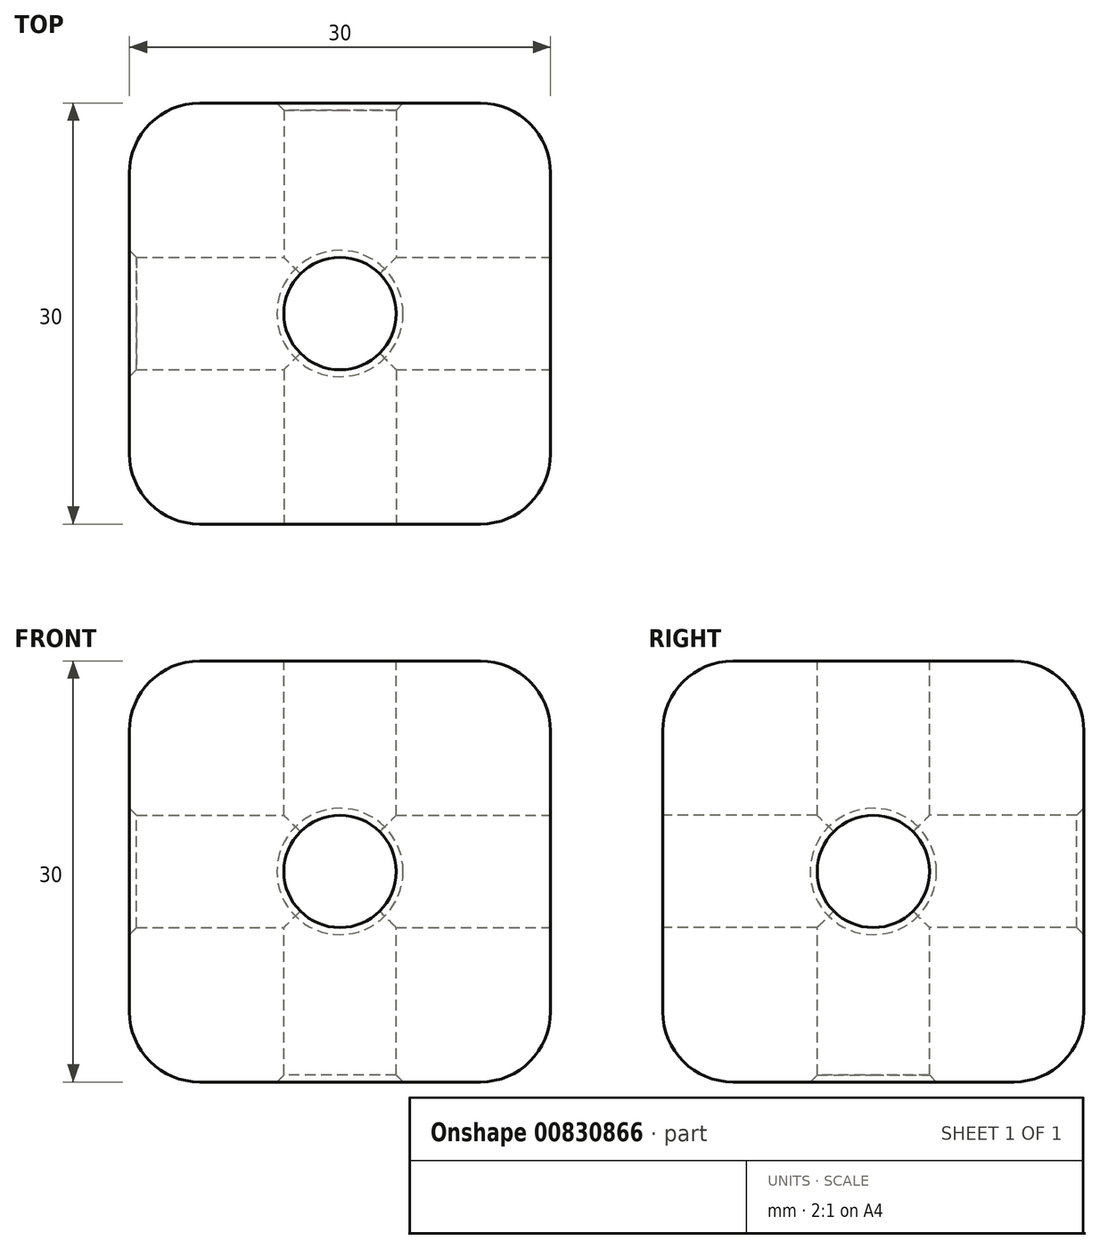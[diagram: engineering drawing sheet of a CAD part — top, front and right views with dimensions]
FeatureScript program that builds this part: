
annotation { "Feature Type Name" : "Feature", "Feature Type Description" : "" }
export const myFeature = defineFeature(function(context is Context, id is Id, definition is map)
    precondition{}
    {
        {
            var Q0;
            Q0=qCreatedBy(makeId("Front.planeOp"),FACE);
            var sketch = newSketch(context, id + "F0", { "sketchPlane" : qUnion([Q0])});
            skLineSegment(sketch, "E0.bottom", {"start": v(-15, 15) * mm, "end": v(15, 15) * mm});
            skLineSegment(sketch, "E0.top", {"start": v(-15, -15) * mm, "end": v(15, -15) * mm});
            skLineSegment(sketch, "E0.left", {"start": v(-15, 15) * mm, "end": v(-15, -15) * mm});
            skLineSegment(sketch, "E0.right", {"start": v(15, 15) * mm, "end": v(15, -15) * mm});
            skPoint(sketch, "E0.middle", {"position": v(0, 0) * mm});
            skSolve(sketch);
        }
        {
            var Q0;
            Q0 = qSketchRegion(id + "F0", true);
            extrude(context, id + "F1", {"entities" : qUnion([Q0]), "depth" : 30 * mm, "offsetDistance" : 25 * mm, "symmetric" : true});
        }
        {
            var Q0;
            Q0=makeQuery(id+"F1.opExtrude","CAP_FACE",FACE,{"disambiguationData":[OSD([sQuery(id+"F0.wireOp",EDGE,"E0.bottom"),sQuery(id+"F0.wireOp",EDGE,"E0.top"),sQuery(id+"F0.wireOp",EDGE,"E0.left"),sQuery(id+"F0.wireOp",EDGE,"E0.right")])],"isStart":false});
            var sketch = newSketch(context, id + "F2", { "sketchPlane" : qUnion([Q0])});
            skCircle(sketch, "E1", {"center": v(0, 0) * mm, "radius": 4 * mm});
            skSolve(sketch);
        }
        {
            var Q0;
            Q0 = qSketchRegion(id + "F2", true);
            var Q1;
            Q1=sQuery(id+"F2.wireOp",EDGE,"E1");
            extrude(context, id + "F3", {"entities" : qUnion([Q0]), "operationType" : NewBodyOperationType.REMOVE, "surfaceEntities" : qUnion([Q1]), "endBound" : BoundingType.THROUGH_ALL, "oppositeDirection" : true, "depth" : 25 * mm, "offsetDistance" : 25 * mm});
        }
        {
            var Q0;
            Q0=makeQuery(id+"F1.opExtrude","SWEPT_FACE",FACE,{"disambiguationData":[OSD([sQuery(id+"F0.wireOp",EDGE,"E0.right")])]});
            var sketch = newSketch(context, id + "F4", { "sketchPlane" : qUnion([Q0])});
            skCircle(sketch, "E2", {"center": v(0, 0) * mm, "radius": 4 * mm});
            skSolve(sketch);
        }
        {
            var Q0;
            Q0 = qSketchRegion(id + "F4", true);
            var Q1;
            Q1=sQuery(id+"F4.wireOp",EDGE,"E2");
            extrude(context, id + "F5", {"entities" : qUnion([Q0]), "operationType" : NewBodyOperationType.REMOVE, "surfaceEntities" : qUnion([Q1]), "endBound" : BoundingType.THROUGH_ALL, "oppositeDirection" : true, "depth" : 25 * mm, "offsetDistance" : 25 * mm});
        }
        {
            var Q0;
            Q0=makeQuery(id+"F1.opExtrude","SWEPT_FACE",FACE,{"disambiguationData":[OSD([sQuery(id+"F0.wireOp",EDGE,"E0.bottom")])]});
            var sketch = newSketch(context, id + "F6", { "sketchPlane" : qUnion([Q0])});
            skCircle(sketch, "E3", {"center": v(0, 0) * mm, "radius": 4 * mm});
            skSolve(sketch);
        }
        {
            var Q0;
            Q0 = qSketchRegion(id + "F6", true);
            extrude(context, id + "F7", {"entities" : qUnion([Q0]), "operationType" : NewBodyOperationType.REMOVE, "endBound" : BoundingType.THROUGH_ALL, "oppositeDirection" : true, "depth" : 25 * mm, "offsetDistance" : 25 * mm});
        }
        {
            var Q0;
            Q0=makeQuery(id+"F1.opExtrude","SWEPT_EDGE",EDGE,{"disambiguationData":[OSD([sQuery(id+"F0.wireOp",EDGE,"E0.bottom"),sQuery(id+"F0.wireOp",EDGE,"E0.right")])]});
            var Q1;
            Q1=makeQuery(id+"F1.opExtrude","CAP_EDGE",EDGE,{"disambiguationData":[OSD([sQuery(id+"F0.wireOp",EDGE,"E0.bottom")])],"isStart":false});
            var Q2;
            Q2=makeQuery(id+"F1.opExtrude","CAP_EDGE",EDGE,{"disambiguationData":[OSD([sQuery(id+"F0.wireOp",EDGE,"E0.right")])],"isStart":false});
            var Q3;
            Q3=makeQuery(id+"F1.opExtrude","CAP_EDGE",EDGE,{"disambiguationData":[OSD([sQuery(id+"F0.wireOp",EDGE,"E0.top")])],"isStart":false});
            var Q4;
            Q4=makeQuery(id+"F1.opExtrude","CAP_EDGE",EDGE,{"disambiguationData":[OSD([sQuery(id+"F0.wireOp",EDGE,"E0.left")])],"isStart":false});
            var Q5;
            Q5=makeQuery(id+"F1.opExtrude","CAP_EDGE",EDGE,{"disambiguationData":[OSD([sQuery(id+"F0.wireOp",EDGE,"E0.right")])],"isStart":true});
            var Q6;
            Q6=makeQuery(id+"F1.opExtrude","CAP_EDGE",EDGE,{"disambiguationData":[OSD([sQuery(id+"F0.wireOp",EDGE,"E0.bottom")])],"isStart":true});
            var Q7;
            Q7=makeQuery(id+"F1.opExtrude","CAP_EDGE",EDGE,{"disambiguationData":[OSD([sQuery(id+"F0.wireOp",EDGE,"E0.left")])],"isStart":true});
            var Q8;
            Q8=makeQuery(id+"F1.opExtrude","CAP_EDGE",EDGE,{"disambiguationData":[OSD([sQuery(id+"F0.wireOp",EDGE,"E0.top")])],"isStart":true});
            var Q9;
            Q9=makeQuery(id+"F1.opExtrude","SWEPT_EDGE",EDGE,{"disambiguationData":[OSD([sQuery(id+"F0.wireOp",EDGE,"E0.bottom"),sQuery(id+"F0.wireOp",EDGE,"E0.left")])]});
            var Q10;
            Q10=makeQuery(id+"F1.opExtrude","SWEPT_EDGE",EDGE,{"disambiguationData":[OSD([sQuery(id+"F0.wireOp",EDGE,"E0.top"),sQuery(id+"F0.wireOp",EDGE,"E0.left")])]});
            var Q11;
            Q11=makeQuery(id+"F1.opExtrude","SWEPT_EDGE",EDGE,{"disambiguationData":[OSD([sQuery(id+"F0.wireOp",EDGE,"E0.top"),sQuery(id+"F0.wireOp",EDGE,"E0.right")])]});
            fillet(context, id + "F8", {"entities" : qUnion([Q0, Q1, Q2, Q3, Q4, Q5, Q6, Q7, Q8, Q9, Q10, Q11]), "radius" : 5 * mm, "tangentPropagation" : true, "allowEdgeOverflow" : false});
        }
        {
            var Q0;
            Q0=makeQuery(id+"F7.boolean.opBoolean","COPY",EDGE,{"derivedFrom":makeQuery(id+"F7.opExtrude","CAP_EDGE",EDGE,{"disambiguationData":[OSD([sQuery(id+"F6.wireOp",EDGE,"E3")])],"isStart":true})});
            var Q1;
            Q1=makeQuery(id+"F3.boolean.opBoolean","COPY",EDGE,{"derivedFrom":makeQuery(id+"F3.opExtrude","CAP_EDGE",EDGE,{"disambiguationData":[OSD([sQuery(id+"F2.wireOp",EDGE,"E1")])],"isStart":true})});
            var Q2;
            Q2=makeQuery(id+"F5.boolean.opBoolean","COPY",EDGE,{"derivedFrom":makeQuery(id+"F5.opExtrude","CAP_EDGE",EDGE,{"disambiguationData":[OSD([sQuery(id+"F4.wireOp",EDGE,"E2")])],"isStart":true})});
            var Q3;
            Q3=makeQuery(id+"F3.boolean.opBoolean","INTERSECT",EDGE,{"derivedFrom":[makeQuery(id+"F1.opExtrude","CAP_FACE",FACE,{"disambiguationData":[OSD([sQuery(id+"F0.wireOp",EDGE,"E0.bottom"),sQuery(id+"F0.wireOp",EDGE,"E0.top"),sQuery(id+"F0.wireOp",EDGE,"E0.left"),sQuery(id+"F0.wireOp",EDGE,"E0.right")])],"isStart":true}),makeQuery(id+"F3.opExtrude","SWEPT_FACE",FACE,{"disambiguationData":[OSD([sQuery(id+"F2.wireOp",EDGE,"E1")])]})]});
            var Q4;
            Q4=makeQuery(id+"F5.boolean.opBoolean","INTERSECT",EDGE,{"derivedFrom":[makeQuery(id+"F1.opExtrude","SWEPT_FACE",FACE,{"disambiguationData":[OSD([sQuery(id+"F0.wireOp",EDGE,"E0.left")])]}),makeQuery(id+"F5.opExtrude","SWEPT_FACE",FACE,{"disambiguationData":[OSD([sQuery(id+"F4.wireOp",EDGE,"E2")])]})]});
            var Q5;
            Q5=makeQuery(id+"F7.boolean.opBoolean","INTERSECT",EDGE,{"derivedFrom":[makeQuery(id+"F1.opExtrude","SWEPT_FACE",FACE,{"disambiguationData":[OSD([sQuery(id+"F0.wireOp",EDGE,"E0.top")])]}),makeQuery(id+"F7.opExtrude","SWEPT_FACE",FACE,{"disambiguationData":[OSD([sQuery(id+"F6.wireOp",EDGE,"E3")])]})]});
            chamfer(context, id + "F9", {"entities" : qUnion([Q0, Q1, Q2, Q3, Q4, Q5]), "width" : 0.5 * mm, "tangentPropagation" : true});
        }
    });
